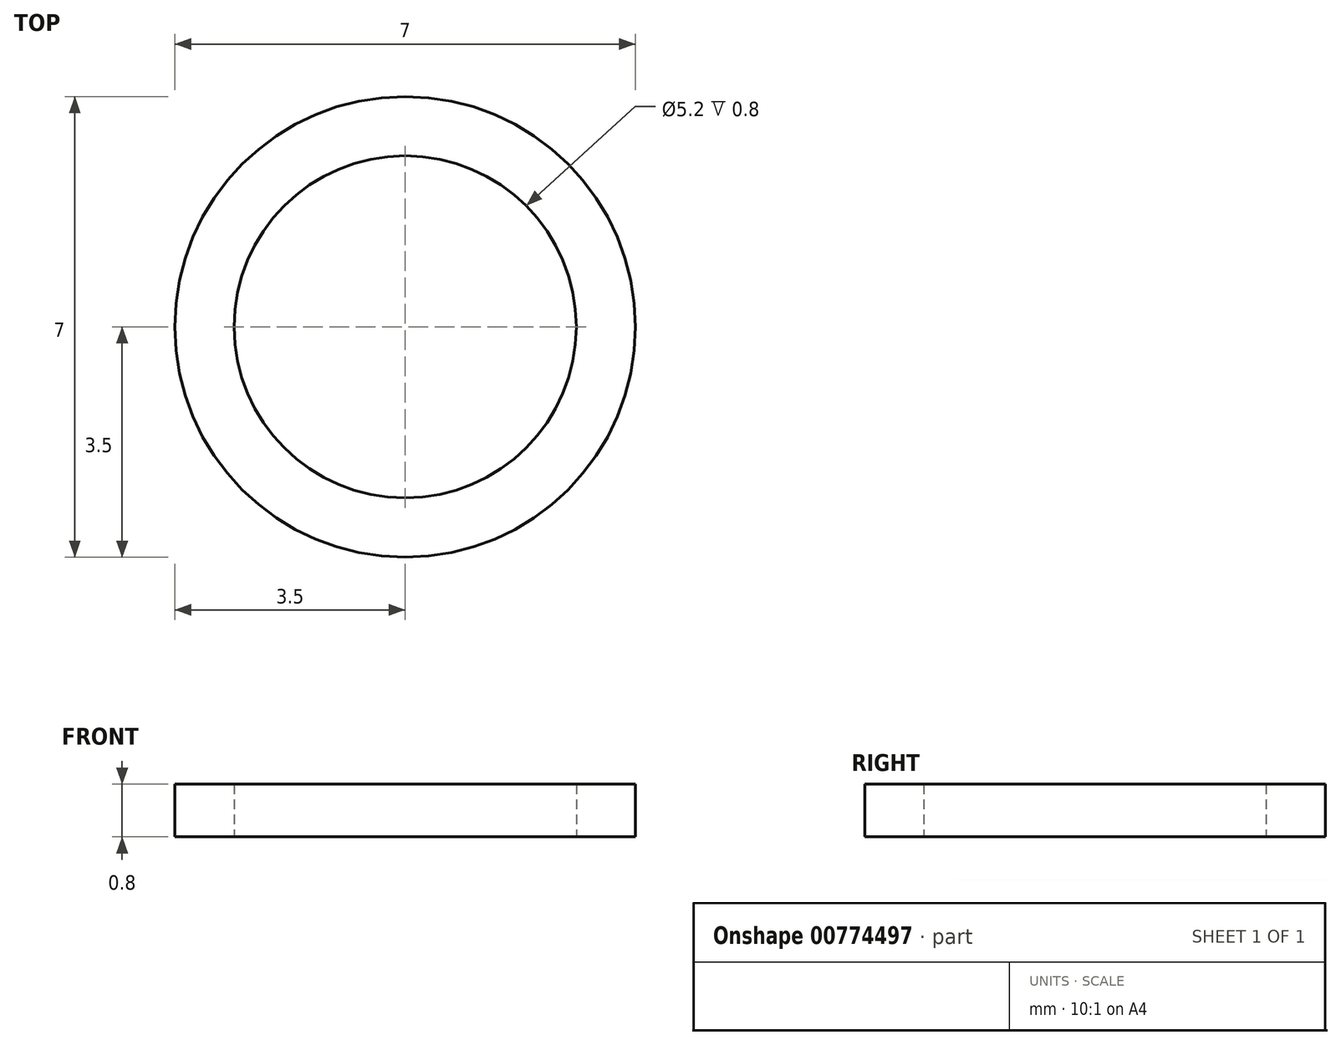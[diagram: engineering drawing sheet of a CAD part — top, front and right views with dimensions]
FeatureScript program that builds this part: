
annotation { "Feature Type Name" : "Feature", "Feature Type Description" : "" }
export const myFeature = defineFeature(function(context is Context, id is Id, definition is map)
    precondition{}
    {
        {
            var Q0;
            Q0=qCreatedBy(makeId("Top.planeOp"),FACE);
            var sketch = newSketch(context, id + "F0", { "sketchPlane" : qUnion([Q0])});
            skCircle(sketch, "E0", {"center": v(0, 0) * mm, "radius": 3.5 * mm});
            skCircle(sketch, "E1", {"center": v(0, 0) * mm, "radius": 2.6 * mm});
            skSolve(sketch);
        }
        {
            var Q0;
            Q0 = qSketchRegion(id + "F0", true);
            extrude(context, id + "F1", {"entities" : qUnion([Q0]), "depth" : 0.8 * mm, "offsetDistance" : 25 * mm});
        }
    });
